# Revit family: Pendant CLED10-13
name_source: partatom
category: Lighting Fixtures
revit_build: Autodesk Revit 2014 (Build: 20130709_2115(x64)
units: mm (PartAtom-declared; Revit-internal decimal feet)

## types (5) — shared parameters
ANSI Lamp Spec = Default - Load Type Catalog
Absolute Color Temperature = 0 K
Anchor Bolts = Default - Load Type Catalog
Apparent Load = 0 VA
Assembly Code = D5020200
Avg Rated Life - TM21 Life Expectancy = Default - Load Type Catalog
BUG Rating = Default - Load Type Catalog
Ballast / Driver Circuit = Default - Load Type Catalog
Ballast ID / ANSI Spec = Default - Load Type Catalog
Base Configuration = Default - Load Type Catalog
Beam Efficiency % = Default - Load Type Catalog
Bolt Circle = Default - Load Type Catalog
CIE Type = Default - Load Type Catalog
CRI 9 = Default - Load Type Catalog
CRI a = Default - Load Type Catalog
Connector Description = Default - Load Type Catalog
Cutoff Classification = Default - Load Type Catalog
Data Datecode = Date Revit Family Type was Created
Description = Default - Load Type Catalog
Field Efficiency = Default - Load Type Catalog
Fixture EPA Rating = Default - Load Type Catalog
Fixture Finish = Metal-RAB Lighting-Aluminum-White
Fixture Weight lbs. = Default - Load Type Catalog
Glass = <By Category>
IES Classification = Default - Load Type Catalog
IP Rating = Default - Load Type Catalog
Initial Source Lumens = 0 lm
Input Wattage = 0 W
Keynote = Division 26
Lamp = Default - Load Type Catalog
Lamp Base = Default - Load Type Catalog
Lamp Envelop = Default - Load Type Catalog
Lensing / Control Media = Default - Load Type Catalog
Longitudinal Classification = Default - Load Type Catalog
Lumens per Watt = 0 lm/W
Luminiare Efficacy Rating LER = 0 lm/W
Luminious Aperture Appearance = Glass-RAB Lighting-LED ON
Manufacturer = RAB Lighting, Inc.
Master Foramt 2004 (Keynote) = Default - Load Type Catalog
Masterformat 2004 Divison of Work = Default - Load Type Catalog
Max Ambient Temp = 104 °F
Mean Source Lumens or L70 Point = 0 lm
Min Starting Temp = -40 °F
Model = Default - Load Type Catalog
Mounting Configuration = Default - Load Type Catalog
NEMA Type = Default - Load Type Catalog
Nominal Color Temperature = 0 K
Nominal Wattage = 0 W
Number of Drivers = Default - Load Type Catalog
Operating Amps = 0 A
Photometric File Name = Default - Load Type Catalog
Product Description = Default - Load Type Catalog
Product Line = Default - Load Type Catalog
Product Model Number = Default - Load Type Catalog
RAB Ballast / Driver ID = Default - Load Type Catalog
Source = Default - Load Type Catalog
Starting Amps = 0 A
Surge Protection kV = 0 V
THD = Default - Load Type Catalog
Total Lumnaire Efficiency = Default - Load Type Catalog
Type Comments = Default - Load Type Catalog
UL / ULC Listing = Default - Load Type Catalog
URL = www.rabled.com
URL Alternate 1 = www.rabweb.com
URL Alternate 2 = www.rabweb.com
Uniformat II (Assembly Code) = Default - Load Type Catalog
Uniformat II Description = Default - Load Type Catalog
Voltage = 0 V
Wattage Comments = 0
zero-valued in all types: Ballast Factor, Cost, Horizontal Beam Angle Degrees, Horizontial Field Angle Degrees, Spacing Criteria 0-180, Spacing Criteria 90-270, Spacing Criteria Diagonal, Vertical Beam Angle Degrees, Vertical Field Angle Degrees

## per-type parameters (varying)
| type | Default Elevation |
| PLED10 - Cool | 1' - 0" |
| PLED10Y - Warm | 0' - 0" |
| PLED13 | 0' - 0" |
| PLED13N | 0' - 0" |
| PLED13Y | 0' - 0" |

## geometry (parser evidence)
native form markers: Sweep x17
no freeform markers — native parametric forms only
